# Revit family: Hager-Type B SP&N Distribution Boards-Surface_mounted-IP3X-With_Cover-With_DIN-Hosted-GB-en
name_source: partatom
category: Electrical Equipment
units: mm (PartAtom-declared; Revit-internal decimal feet)

## family parameters
Cut with Voids When Loaded = No
Host = Face
Maintain Annotation Orientation = Yes
Panel Configuration = Two Columns, Circuits Across
Part Type = Panelboard
Room Calculation Point = No
Round Connector Dimension = Use Diameter
Shared = No

## types (26) — shared parameters
BC_MODEL_ID = 1554197
BC_OBJECT_ID = 513820
BC_OBJECT_VERSION = #1
Code hager = ADD-EC000214_EU
EF000003 - Mounting method = Surface mounted
EF000008 - Width = 465 mm  [stored 1.52559 ft]
EF000024 - UV resistant = No
EF000116 - RAL number = 7035
EF000118 - With mounting plate = No
EF001062 - EMC-version = No
EF001134 - With DIN-rail = Yes
EF002950 - Width in number of modular spacings = 16
EF005474 - Degree of protection (IP rating) = IP3X
EF015776 - Earthing terminal block = Yes
EF015941 - Signal passing door = No
ETIM class code = EC000214
ETIM class name = Small distribution board
HG000001-Number of columns = 1
HG000002-With door or cover = Yes
HG000003-Range = Type B SP&N Distribution Boards
HG000005-Thickness = 2 mm  [stored 0.00656168 ft]
HG000006-Flush mounted = No
HG000009-Double swing door = No
HG000010-Asymmetric doors = No
HG000011-Empty rows from bottom = No
HG000012-Door swing angle = 90.00°
HG000013-Door on the left = No
HG000014-Door on the right = Yes
HG000015-Clearance visibility = Yes
HG000016-Door 3D visibility = Yes
HG000017-Distance between poles = 18 mm  [stored 0.0590551 ft]
HG000060-RAL-number = 7035
HG000099-Onfly Template ID = 507532
HGEF002950-Width in number of modular spacings = 16
Manufacturer = Hager
Name = Type B SP&N Distribution Boards-Surface_mounted-IP3X-With_Cover-With_DIN-GB
Name BIM&CO = Electricity
Name hager = ADD_Enclosures_EC000214
Uniformat = Low Tension Service & Dist.
Uniformat code = D501001
zero-valued in all types: Default Elevation, EF000218 - Recess depth, EF000332 - Recess height, EF000846 - Recess width, EF001131 - Internal depth, HG000007-Number of empty columns, HG000008-Number of empty rows

## per-type parameters (varying)
| type | BC_VARIANT_ID | EF000007 - Colour | EF000040 - Height | EF000049 - Depth | EF000266 - Number of rows | EF001088 - Extension possible | EF004462 - Type of closure | EF006244 - Transparent cover/door | EF006306 - With lock | EF015777 - Neutral terminal block | HG000004-Manufacturer reference | HGEF000266-Number of rows |
| Type B SP&N Distribution Boards-Surface_mounted_W465_H500_D132_16_Modular_Spacing-JK104BDFA3 | 1178547 | Grey | 500 mm  [stored 1.64042 ft] | 132 mm  [stored 0.433071 ft] | 2 | Yes |  | No | Yes | Yes | JK104BDFA3 | 2 |
| Type B SP&N Distribution Boards-Surface_mounted_W465_H500_D132_16_Modular_Spacing-JK104BDFG | 1178548 | Grey | 500 mm  [stored 1.64042 ft] | 132 mm  [stored 0.433071 ft] | 2 | Yes |  | Yes | Yes | Yes | JK104BDFG | 2 |
| Type B SP&N Distribution Boards-Surface_mounted_W465_H550_D132_16_Modular_Spacing-JK106BDFA3 | 1178549 | Grey | 550 mm | 132 mm  [stored 0.433071 ft] | 2 | Yes |  | No | Yes | Yes | JK106BDFA3 | 2 |
| Type B SP&N Distribution Boards-Surface_mounted_W465_H550_D132_16_Modular_Spacing-JK106BDFG | 1178550 | Grey | 550 mm | 132 mm  [stored 0.433071 ft] | 2 | Yes |  | Yes | Yes | Yes | JK106BDFG | 2 |
| Type B SP&N Distribution Boards-Surface_mounted_W465_H625_D132_16_Modular_Spacing-JK108BDFA3 | 1178551 | Grey | 625 mm  [stored 2.05052 ft] | 132 mm  [stored 0.433071 ft] | 3 | Yes |  | No | Yes | Yes | JK108BDFA3 | 3 |
| Type B SP&N Distribution Boards-Surface_mounted_W465_H625_D132_16_Modular_Spacing-JK108BDFG | 1178552 | Grey | 625 mm  [stored 2.05052 ft] | 132 mm  [stored 0.433071 ft] | 3 | Yes |  | No | Yes | Yes | JK108BDFG | 3 |
| Type B SP&N Distribution Boards-Surface_mounted_W465_H850_D132_16_Modular_Spacing-JK112BDFA3 | 1178553 | Grey | 850 mm  [stored 2.78871 ft] | 132 mm  [stored 0.433071 ft] | 4 | Yes |  | No | Yes | Yes | JK112BDFA3 | 4 |
| Type B SP&N Distribution Boards-Surface_mounted_W465_H850_D132_16_Modular_Spacing-JK112BDFG | 1178554 | Grey | 850 mm  [stored 2.78871 ft] | 132 mm  [stored 0.433071 ft] | 4 | Yes |  | No | Yes | Yes | JK112BDFG | 4 |
| Type B SP&N Distribution Boards-Surface_mounted_W465_H950_D132_16_Modular_Spacing-JK116BDFA3 | 1178555 | Grey | 950 mm  [stored 3.1168 ft] | 132 mm  [stored 0.433071 ft] | 5 | Yes |  | No | Yes | Yes | JK116BDFA3 | 5 |
| Type B SP&N Distribution Boards-Surface_mounted_W465_H950_D132_16_Modular_Spacing-JK116BDFG | 1178556 | Grey | 950 mm  [stored 3.1168 ft] | 132 mm  [stored 0.433071 ft] | 5 | Yes |  | No | Yes | Yes | JK116BDFG | 5 |
| Type B SP&N Distribution Boards-Surface_mounted_W465_H300_D165_16_Modular_Spacing-JK116EA3 | 1178557 | Grey | 300 mm | 165 mm  [stored 0.541339 ft] | 1 | Yes |  | No | Yes | Yes | JK116EA3 | 1 |
| Type B SP&N Distribution Boards-Surface_mounted_W465_H950_D165_16_Modular_Spacing-JK208BDFA3 | 1178558 | Grey | 950 mm  [stored 3.1168 ft] | 165 mm  [stored 0.541339 ft] | 5 | Yes |  | No | Yes | Yes | JK208BDFA3 | 5 |
| Type B SP&N Distribution Boards-Surface_mounted_W465_H950_D165_16_Modular_Spacing-JK208BDFG | 1178559 | Grey | 950 mm  [stored 3.1168 ft] | 165 mm  [stored 0.541339 ft] | 5 | Yes |  | No | Yes | Yes | JK208BDFG | 5 |
| Type B SP&N Distribution Boards-Surface_mounted_W465_H1100_D165_16_Modular_Spacing-JK212BDFA3 | 1178560 | Grey | 1100 mm | 165 mm  [stored 0.541339 ft] | 5 | Yes |  | No | Yes | Yes | JK212BDFA3 | 5 |
| Type B SP&N Distribution Boards-Surface_mounted_W465_H1100_D165_16_Modular_Spacing-JK212BDFG | 1178561 | Grey | 1100 mm | 165 mm  [stored 0.541339 ft] | 5 | Yes |  | No | Yes | Yes | JK212BDFG | 5 |
| Type B SP&N Distribution Boards-Surface_mounted_W465_H1250_D166_16_Modular_Spacing-JK216BDFA3 | 1178562 | Grey | 1250 mm  [stored 4.10105 ft] | 166 mm  [stored 0.544619 ft] | 6 | Yes |  | No | Yes | Yes | JK216BDFA3 | 6 |
| Type B SP&N Distribution Boards-Surface_mounted_W465_H1250_D165_16_Modular_Spacing-JK216BDFG | 1178563 | Grey | 1250 mm  [stored 4.10105 ft] | 165 mm  [stored 0.541339 ft] | 6 | Yes |  | No | Yes | Yes | JK216BDFG | 6 |
| Type B SP&N Distribution Boards-Surface_mounted_W465_H300_D165_16_Modular_Spacing-JK216E | 1178564 |  | 300 mm | 165 mm  [stored 0.541339 ft] | 1 | No |  | No | No | No | JK216E | 1 |
| Type B SP&N Distribution Boards-Surface_mounted_W465_H300_D166_16_Modular_Spacing-JK216EA3 | 1178565 |  | 300 mm | 166 mm  [stored 0.544619 ft] | 1 | No |  | No | No | Yes | JK216EA3 | 1 |
| Type B SP&N Distribution Boards-Surface_mounted_W465_H1400_D166_16_Modular_Spacing-JK218BDFA3 | 1178566 | Grey | 1400 mm  [stored 4.59318 ft] | 166 mm  [stored 0.544619 ft] | 7 | Yes |  | No | Yes | Yes | JK218BDFA3 | 7 |
| Type B SP&N Distribution Boards-Surface_mounted_W465_H1400_D166_16_Modular_Spacing-JK218BDFG | 1178567 | Grey | 1400 mm  [stored 4.59318 ft] | 166 mm  [stored 0.544619 ft] | 7 | Yes |  | No | Yes | Yes | JK218BDFG | 7 |
| Type B SP&N Distribution Boards-Surface_mounted_W465_H1550_D165_16_Modular_Spacing-JK224BDFA3 | 1178568 | Grey | 1550 mm  [stored 5.0853 ft] | 165 mm  [stored 0.541339 ft] | 8 | Yes |  | No | Yes | Yes | JK224BDFA3 | 8 |
| Type B SP&N Distribution Boards-Surface_mounted_W465_H1550_D165_16_Modular_Spacing-JK224BDFG | 1178569 | Grey | 1550 mm  [stored 5.0853 ft] | 165 mm  [stored 0.541339 ft] | 8 | Yes |  | No | Yes | Yes | JK224BDFG | 8 |
| Type B SP&N Distribution Boards-Surface_mounted_W465_H450_D165_16_Modular_Spacing-JK232E | 1178570 |  | 450 mm  [stored 1.47638 ft] | 165 mm  [stored 0.541339 ft] | 2 | No |  | No | No | Yes | JK232E | 2 |
| Type B SP&N Distribution Boards-Surface_mounted_W465_H450_D165_16_Modular_Spacing-JK232EA3 | 1178571 | Other | 450 mm  [stored 1.47638 ft] | 165 mm  [stored 0.541339 ft] | 2 | No | Other | No | Yes | Yes | JK232EA3 | 2 |
| Type B SP&N Distribution Boards-Surface_mounted_W465_H450_D165_16_Modular_Spacing-JK232EG | 1178572 |  | 450 mm  [stored 1.47638 ft] | 165 mm  [stored 0.541339 ft] | 2 | No |  | No | No | Yes | JK232EG | 2 |

note: column(s) folded — value = type name in every type: Reference

note: [stored X ft] marks values corroborated as IEEE doubles in the binary element streams (Revit-internal decimal feet)

## geometry (parser evidence)
native form markers: Sweep x16
no freeform markers — native parametric forms only
